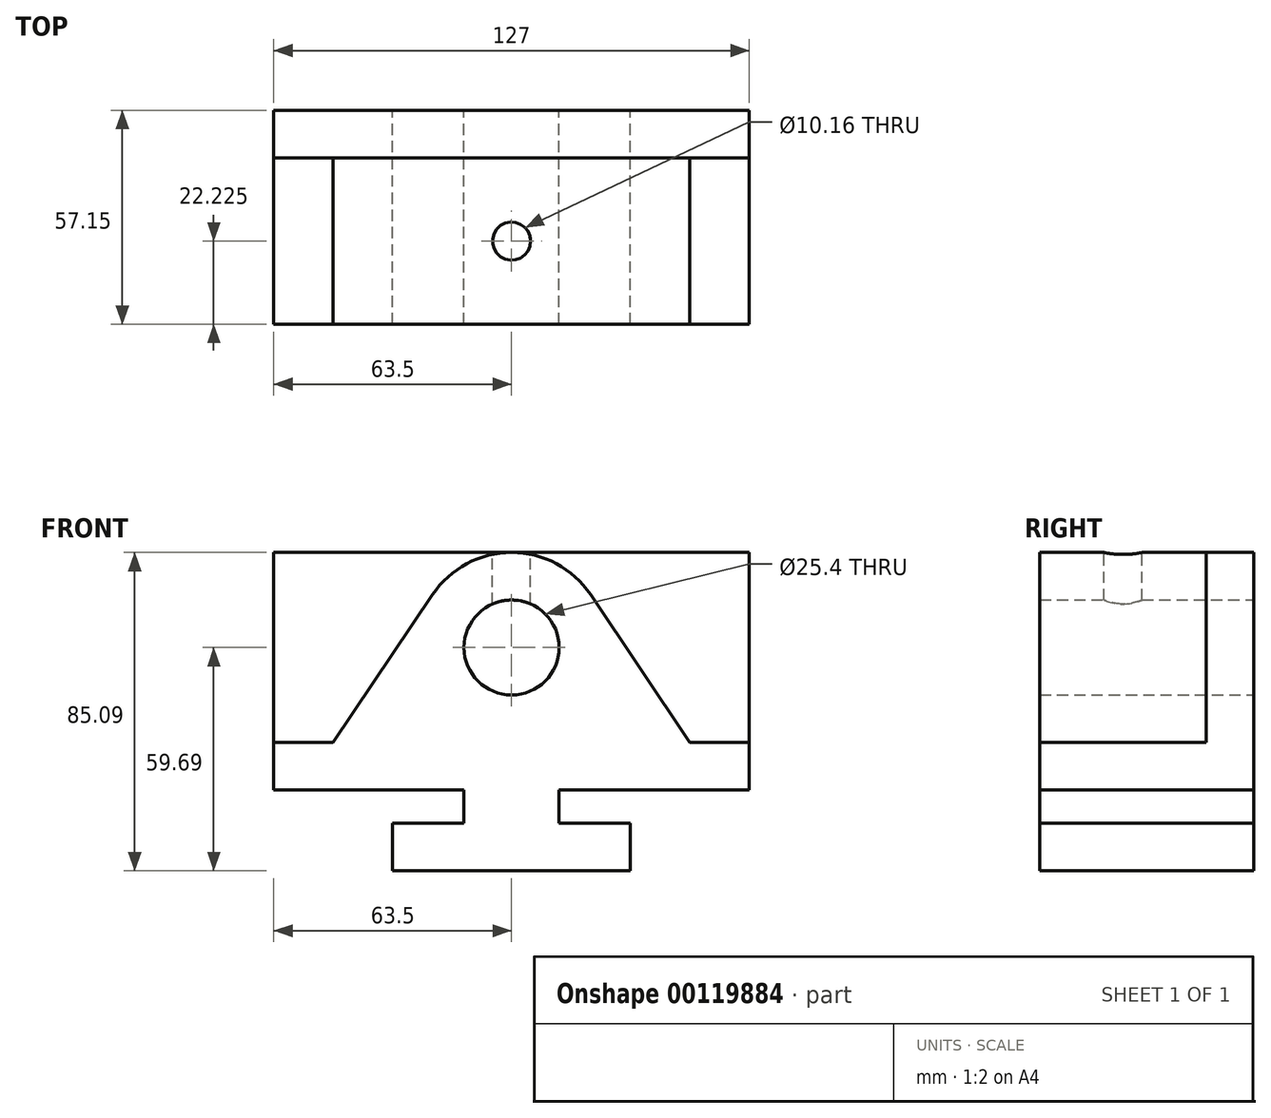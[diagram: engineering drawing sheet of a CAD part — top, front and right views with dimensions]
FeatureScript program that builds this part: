
annotation { "Feature Type Name" : "Feature", "Feature Type Description" : "" }
export const myFeature = defineFeature(function(context is Context, id is Id, definition is map)
    precondition{}
    {
        {
            var Q0;
            Q0=qCreatedBy(makeId("Front.planeOp"),FACE);
            var sketch = newSketch(context, id + "F0", { "sketchPlane" : qUnion([Q0])});
            skLineSegment(sketch, "E0", {"start": v(0, 0) * mm, "end": v(31.75, 0) * mm});
            skLineSegment(sketch, "E1", {"start": v(31.75, 0) * mm, "end": v(31.75, 12.7) * mm});
            skLineSegment(sketch, "E2", {"start": v(31.75, 12.7) * mm, "end": v(12.7, 12.7) * mm});
            skLineSegment(sketch, "E3", {"start": v(12.7, 12.7) * mm, "end": v(12.7, 21.59) * mm});
            skLineSegment(sketch, "E4", {"start": v(12.7, 21.59) * mm, "end": v(63.5, 21.59) * mm});
            skLineSegment(sketch, "E5", {"start": v(63.5, 21.59) * mm, "end": v(63.5, 34.3) * mm});
            skLineSegment(sketch, "E6", {"start": v(0, 0) * mm, "end": v(-31.75, 0) * mm});
            skLineSegment(sketch, "E7", {"start": v(-31.75, 0) * mm, "end": v(-31.75, 12.7) * mm});
            skLineSegment(sketch, "E8", {"start": v(-31.75, 12.7) * mm, "end": v(-12.7, 12.7) * mm});
            skLineSegment(sketch, "E9", {"start": v(-12.7, 12.7) * mm, "end": v(-12.7, 21.59) * mm});
            skLineSegment(sketch, "E10", {"start": v(-12.7, 21.59) * mm, "end": v(-63.5, 21.59) * mm});
            skLineSegment(sketch, "E11", {"start": v(-63.5, 21.59) * mm, "end": v(-63.5, 34.3) * mm});
            skLineSegment(sketch, "E12", {"start": v(-47.63, 34.3) * mm, "end": v(-63.5, 34.3) * mm});
            skLineSegment(sketch, "E13", {"start": v(47.63, 34.3) * mm, "end": v(63.5, 34.3) * mm});
            skLineSegment(sketch, "E14", {"start": v(-47.63, 34.3) * mm, "end": v(-21.1, 73.84) * mm});
            skLineSegment(sketch, "E15", {"start": v(21.1, 73.84) * mm, "end": v(47.63, 34.3) * mm});
            skArc(sketch, "E16", {"start": v(-21.1, 73.84) * mm, "mid": v(0, 85.1) * mm, "end": v(21.1, 73.84) * mm});
            skCircle(sketch, "E17", {"center": v(0, 59.7) * mm, "radius": 12.7 * mm});
            skLineSegment(sketch, "E18", {"start": v(0, 85.1) * mm, "end": v(0, 0) * mm, "construction": true});
            skSolve(sketch);
        }
        {
            var Q0;
            Q0=qCreatedBy(makeId("Front.planeOp"),FACE);
            var sketch = newSketch(context, id + "F1", { "sketchPlane" : qUnion([Q0])});
            skLineSegment(sketch, "E19", {"start": v(-63.5, 34.3) * mm, "end": v(-63.5, 85.1) * mm});
            skLineSegment(sketch, "E20", {"start": v(-63.5, 85.1) * mm, "end": v(63.5, 85.1) * mm});
            skLineSegment(sketch, "E21", {"start": v(63.5, 85.1) * mm, "end": v(63.5, 34.3) * mm});
            skLineSegment(sketch, "E22", {"start": v(63.5, 34.3) * mm, "end": v(-63.5, 34.29) * mm});
            skCircle(sketch, "E23", {"center": v(0, 59.7) * mm, "radius": 12.7 * mm});
            skSolve(sketch);
        }
        {
            var Q0;
            Q0 = qSketchRegion(id + "F0", true);
            extrude(context, id + "F2", {"entities" : qUnion([Q0]), "depth" : 57.15 * mm});
        }
        {
            var Q0;
            Q0 = qSketchRegion(id + "F1", true);
            extrude(context, id + "F3", {"entities" : qUnion([Q0]), "operationType" : NewBodyOperationType.ADD, "depth" : 12.7 * mm});
        }
        {
            var Q0;
            Q0=makeQuery(id+"F3.opExtrude","SWEPT_FACE",FACE,{"disambiguationData":[OSD([sQuery(id+"F1.wireOp",EDGE,"E20")])]});
            var sketch = newSketch(context, id + "F4", { "sketchPlane" : qUnion([Q0])});
            skLineSegment(sketch, "E24", {"start": v(0, 0) * mm, "end": v(0, -34.93) * mm, "construction": true});
            skCircle(sketch, "E25", {"center": v(0, -34.93) * mm, "radius": 5.08 * mm});
            skSolve(sketch);
        }
        {
            var Q0;
            Q0 = qSketchRegion(id + "F4", true);
            extrude(context, id + "F5", {"entities" : qUnion([Q0]), "operationType" : NewBodyOperationType.REMOVE, "oppositeDirection" : true, "depth" : 25.4 * mm});
        }
    });
